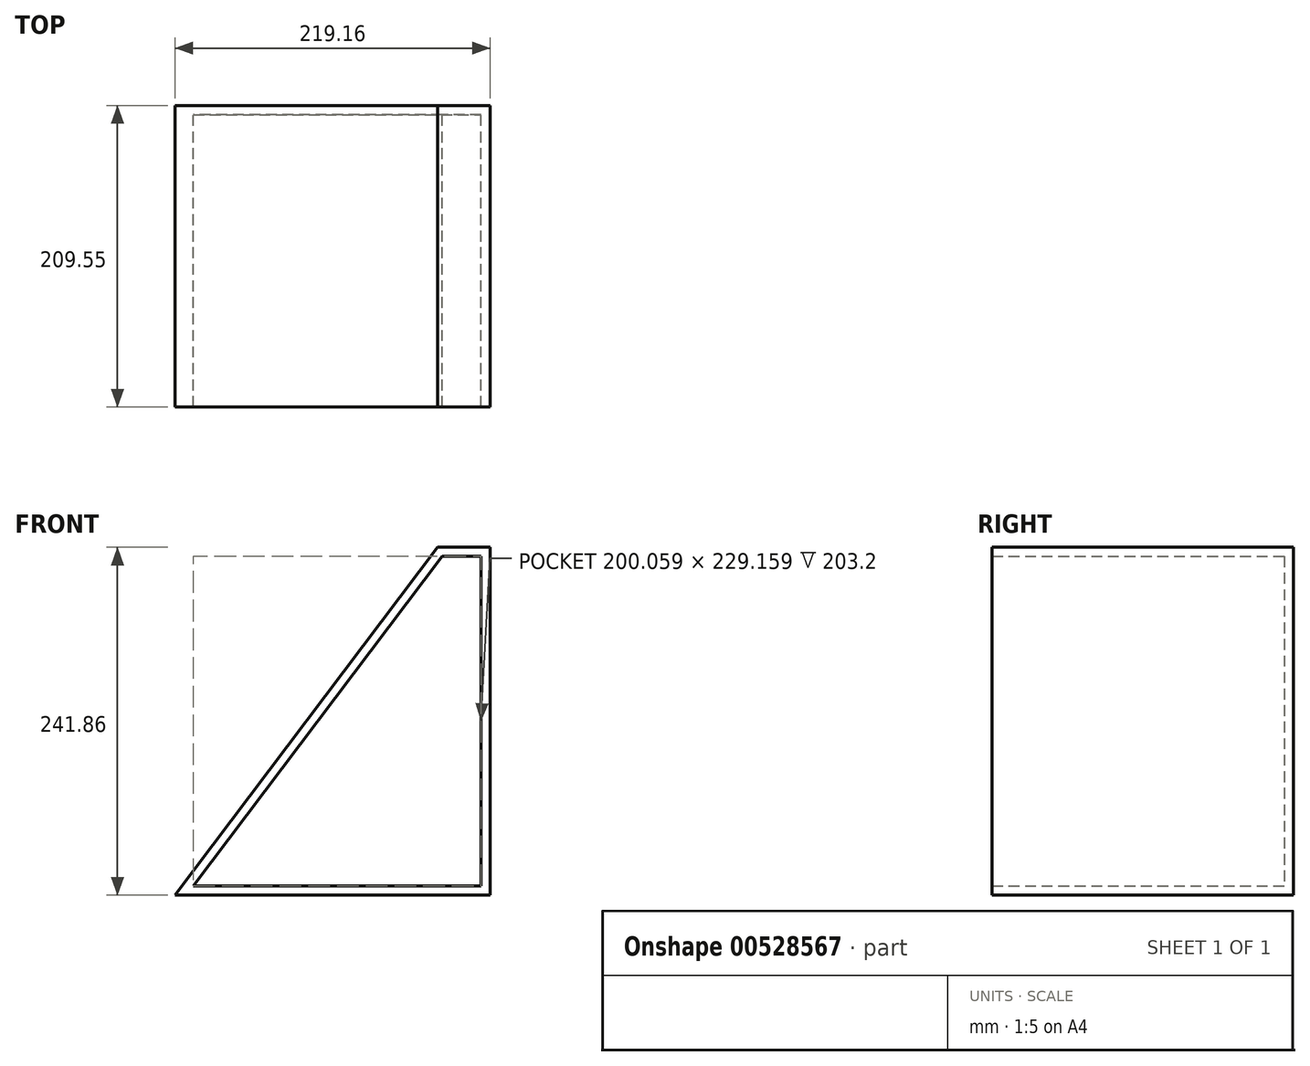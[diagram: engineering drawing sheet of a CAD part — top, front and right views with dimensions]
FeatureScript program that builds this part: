
annotation { "Feature Type Name" : "Feature", "Feature Type Description" : "" }
export const myFeature = defineFeature(function(context is Context, id is Id, definition is map)
    precondition{}
    {
        {
            var Q0;
            Q0=qCreatedBy(makeId("Front.planeOp"),FACE);
            var sketch = newSketch(context, id + "F0", { "sketchPlane" : qUnion([Q0])});
            skLineSegment(sketch, "E0", {"start": v(0, 0) * mm, "end": v(0, 422.71) * mm, "construction": true});
            skLineSegment(sketch, "E1", {"start": v(-147.7, 374.37) * mm, "end": v(0, 374.37) * mm, "construction": true});
            skLineSegment(sketch, "E2", {"start": v(-219.16, 132.5) * mm, "end": v(0, 132.5) * mm, "construction": true});
            skLineSegment(sketch, "E3", {"start": v(0, 422.71) * mm, "end": v(-319.23, 0) * mm, "construction": true});
            skSolve(sketch);
        }
        {
            var Q0;
            Q0=qCreatedBy(makeId("Front.planeOp"),FACE);
            var sketch = newSketch(context, id + "F1", { "sketchPlane" : qUnion([Q0])});
            skLineSegment(sketch, "E4", {"start": v(-219.16, 132.5) * mm, "end": v(0, 132.5) * mm});
            skLineSegment(sketch, "E5", {"start": v(0, 132.5) * mm, "end": v(0, 374.37) * mm});
            skLineSegment(sketch, "E6", {"start": v(0, 374.37) * mm, "end": v(-36.51, 374.37) * mm});
            skLineSegment(sketch, "E7", {"start": v(-36.51, 374.37) * mm, "end": v(-219.16, 132.5) * mm});
            skSolve(sketch);
        }
        {
            var Q0;
            Q0 = qSketchRegion(id + "F1", true);
            extrude(context, id + "F2", {"entities" : qUnion([Q0]), "depth" : 6.35 * mm, "offsetDistance" : 25.4 * mm});
        }
        {
            var Q0;
            Q0=makeQuery(id+"F2.opExtrude","CAP_FACE",FACE,{"disambiguationData":[OSD([sQuery(id+"F1.wireOp",EDGE,"E4"),sQuery(id+"F1.wireOp",EDGE,"E5"),sQuery(id+"F1.wireOp",EDGE,"E6"),sQuery(id+"F1.wireOp",EDGE,"E7")])],"isStart":false});
            var sketch = newSketch(context, id + "F3", { "sketchPlane" : qUnion([Q0])});
            skLineSegment(sketch, "E8", {"start": v(-219.16, 132.5) * mm, "end": v(0, 132.5) * mm});
            skLineSegment(sketch, "E9", {"start": v(0, 132.5) * mm, "end": v(0, 374.37) * mm});
            skLineSegment(sketch, "E10", {"start": v(0, 374.37) * mm, "end": v(-36.51, 374.37) * mm});
            skLineSegment(sketch, "E11", {"start": v(-36.51, 374.37) * mm, "end": v(-219.16, 132.5) * mm});
            skLineSegment(sketch, "E12", {"start": v(-33.35, 368.02) * mm, "end": v(-206.4, 138.86) * mm});
            skLineSegment(sketch, "E13", {"start": v(-206.4, 138.86) * mm, "end": v(-6.35, 138.86) * mm});
            skLineSegment(sketch, "E14", {"start": v(-6.35, 138.86) * mm, "end": v(-6.35, 368.02) * mm});
            skLineSegment(sketch, "E15", {"start": v(-6.35, 368.02) * mm, "end": v(-33.35, 368.02) * mm});
            skSolve(sketch);
        }
        {
            var Q0;
            Q0 = qSketchRegion(id + "F3", true);
            extrude(context, id + "F4", {"entities" : qUnion([Q0]), "operationType" : NewBodyOperationType.ADD, "depth" : 203.2 * mm, "offsetDistance" : 25.4 * mm});
        }
    });
